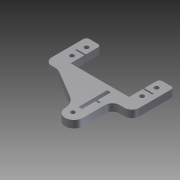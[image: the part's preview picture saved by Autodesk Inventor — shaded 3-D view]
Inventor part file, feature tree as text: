
AUTODESK INVENTOR PART (.ipt)
format: ipt  version: 2012 (Build 160160000, 160)  size: 193,024 bytes
history: native  units: mm
features: sketch x2, extrude x1, hole x1
ambient origin geometry x8: Origin, YZ Plane, XZ Plane, XY Plane, X Axis, Y Axis, Z Axis, Center Point
bodies: Solid1 (feature_tree)
feature tree (4):
  extrude  "Extrusion1"  Depth=60.0mm
  hole  "Hole2"  [1 undecoded]
  sketch  "Sketch1"  dims[d14=5.0mm d15=0.0mm]
  sketch  "Sketch3"  dims[d59=1.25mm d60=2.5mm d61=19.8mm d62=5.0mm d63=9.4mm d64=2.5mm d65=1.0mm d66=1.0mm d67=1.0mm d68=5.0mm d69=10.0mm d70=10.0mm d71=2.0mm d81=40.0mm d82=40.0mm d83=10.0mm d84=10.0mm d88=6.75mm d89=1.25mm d90=2.5mm d91=19.8mm d92=5.0mm d93=9.4mm d94=2.5mm d95=1.0mm d96=1.0mm d97=1.0mm d98=5.0mm d99=10.0mm d100=10.0mm d101=2.0mm d102=10.0mm d103=10.0mm d104=4.5mm d105=4.5mm d106=4.5mm d107=4.5mm d108=4.0mm d109=48.0mm d110=48.0mm d111=40.0mm d112=40.0mm d113=10.0mm d114=10.0mm d115=4.0mm d116=4.0mm d117=4.0mm d118=6.75mm d119=3.0mm d120=6.0mm d121=4.0mm d122=2.0mm d123=90.0deg d124=8.0mm d125=20.594885mm d126=60.0mm d127=33.2mm]
note: 1 required parameter value undecoded (feature->parameter linkage not recoverable at this tier; creation-order binding heuristic only, values carry confidence <= 0.55)
